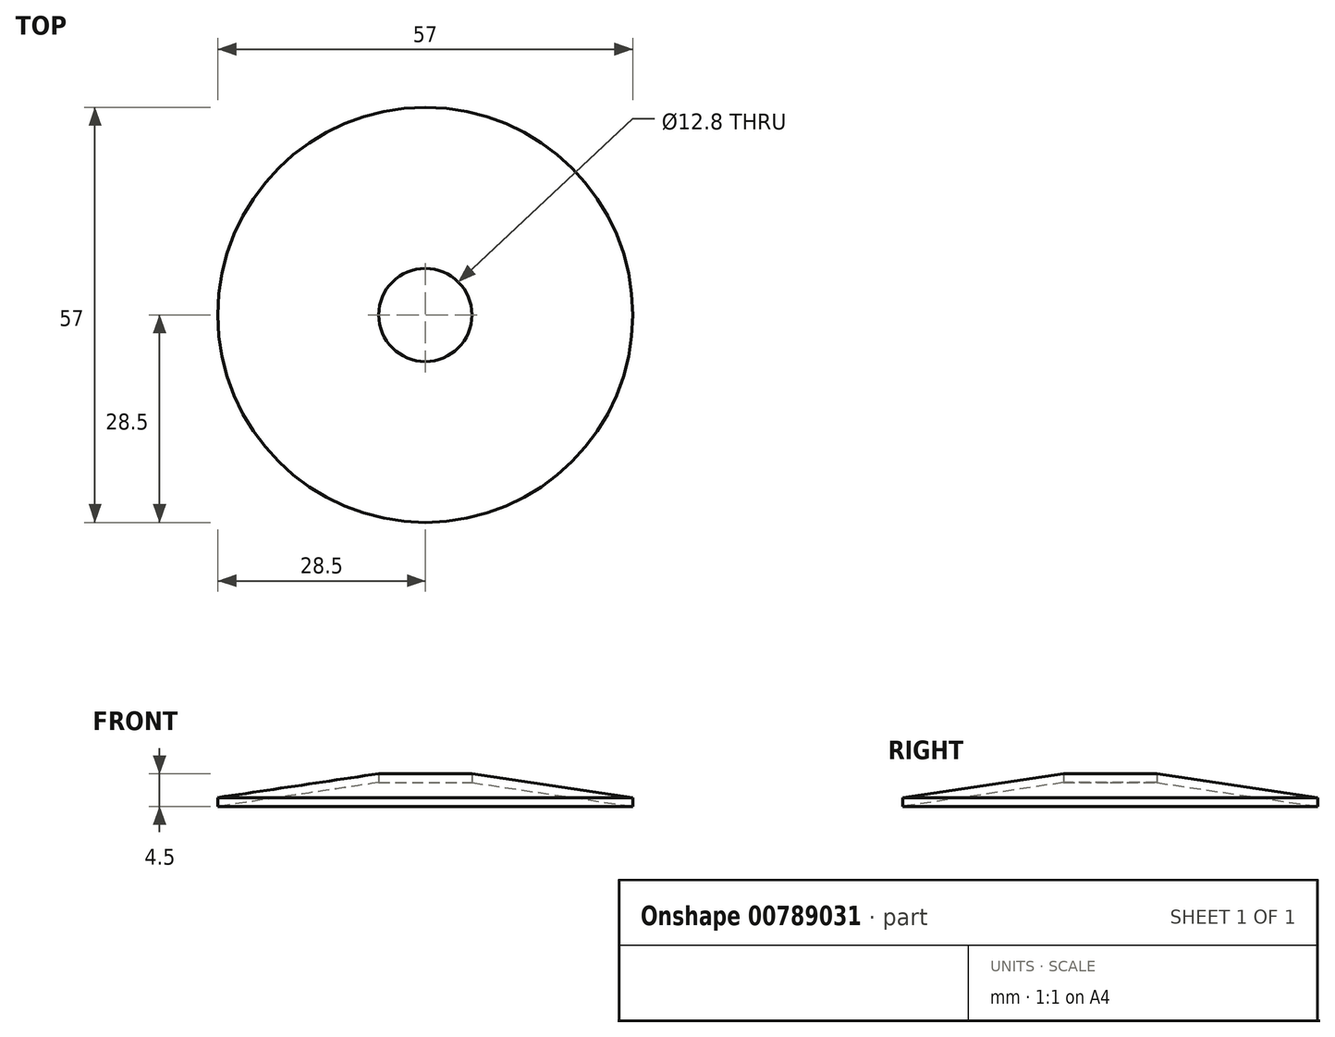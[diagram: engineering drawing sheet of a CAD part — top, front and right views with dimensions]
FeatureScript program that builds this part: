
annotation { "Feature Type Name" : "Feature", "Feature Type Description" : "" }
export const myFeature = defineFeature(function(context is Context, id is Id, definition is map)
    precondition{}
    {
        {
            var Q0;
            Q0=qCreatedBy(makeId("Front.planeOp"),FACE);
            var sketch = newSketch(context, id + "F0", { "sketchPlane" : qUnion([Q0])});
            skLineSegment(sketch, "E0", {"start": v(-6.4, 0) * mm, "end": v(-28.5, -3.28) * mm});
            skLineSegment(sketch, "E1", {"start": v(-28.5, -3.28) * mm, "end": v(-28.5, -4.5) * mm});
            skLineSegment(sketch, "E2", {"start": v(-28.5, -4.5) * mm, "end": v(-6.4, -1.22) * mm});
            skLineSegment(sketch, "E3", {"start": v(-6.4, -1.22) * mm, "end": v(-6.4, 0) * mm});
            skLineSegment(sketch, "E4", {"start": v(0, -14.66) * mm, "end": v(0, 10.83) * mm, "construction": true});
            skSolve(sketch);
        }
        {
            var Q0;
            Q0 = qSketchRegion(id + "F0", true);
            var Q1;
            Q1=sQuery(id+"F0.wireOp",EDGE,"E4");
            revolve(context, id + "F1", {"surfaceOperationType" : NewSurfaceOperationType.NEW, "entities" : qUnion([Q0]), "axis" : qUnion([Q1]), "revolveType" : RevolveType.FULL});
        }
    });
